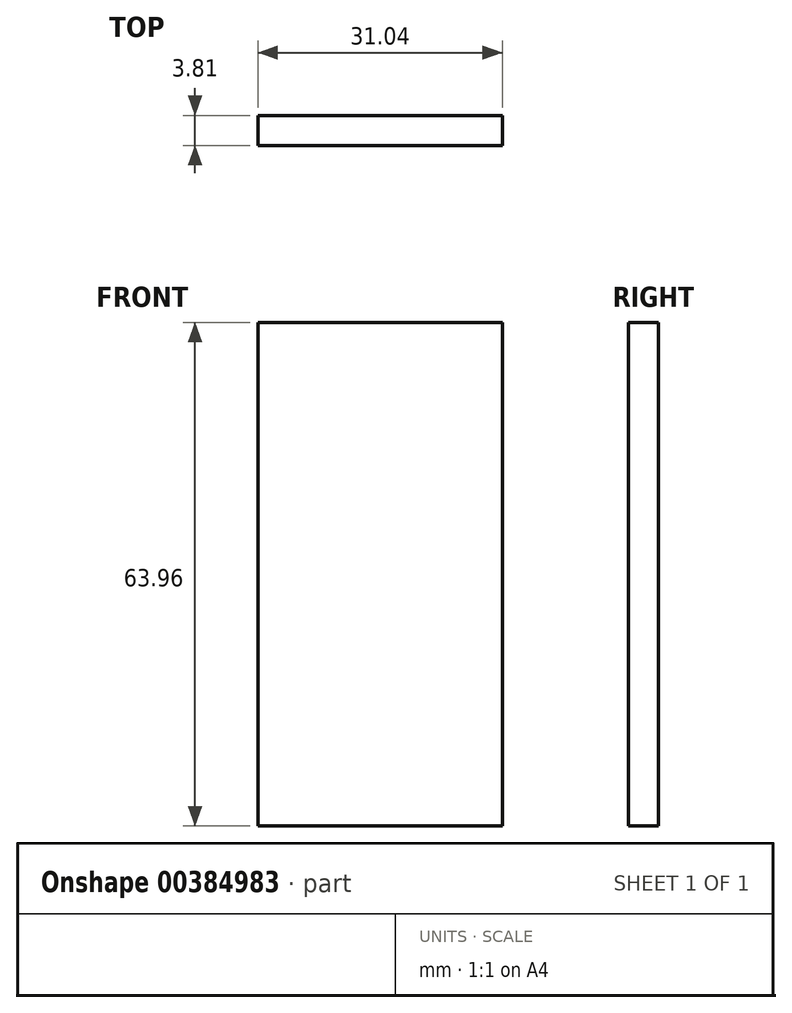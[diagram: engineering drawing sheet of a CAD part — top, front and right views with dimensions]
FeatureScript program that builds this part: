
annotation { "Feature Type Name" : "Feature", "Feature Type Description" : "" }
export const myFeature = defineFeature(function(context is Context, id is Id, definition is map)
    precondition{}
    {
        {
            var Q0;
            Q0=qCreatedBy(makeId("Front.planeOp"),FACE);
            var sketch = newSketch(context, id + "F0", { "sketchPlane" : qUnion([Q0])});
            skLineSegment(sketch, "E0", {"start": v(-29.68, 27.28) * mm, "end": v(-29.68, -36.68) * mm});
            skLineSegment(sketch, "E1", {"start": v(-29.68, -36.68) * mm, "end": v(1.36, -36.68) * mm});
            skLineSegment(sketch, "E2", {"start": v(1.36, -36.68) * mm, "end": v(1.36, 27.28) * mm});
            skLineSegment(sketch, "E3", {"start": v(1.36, 27.28) * mm, "end": v(-29.68, 27.28) * mm});
            skSolve(sketch);
        }
        {
            var Q0;
            Q0=makeQuery(id+"F0.imprint","IMPRINT",FACE,{"disambiguationData":[TD([[makeQuery(id+"F0.imprint","IMPRINT",EDGE,{"derivedFrom":sQuery(id+"F0.wireOp",EDGE,"E0")}),1.0]])]});
            extrude(context, id + "F1", {"entities" : qUnion([Q0]), "depth" : 3.8 * mm});
        }
    });
